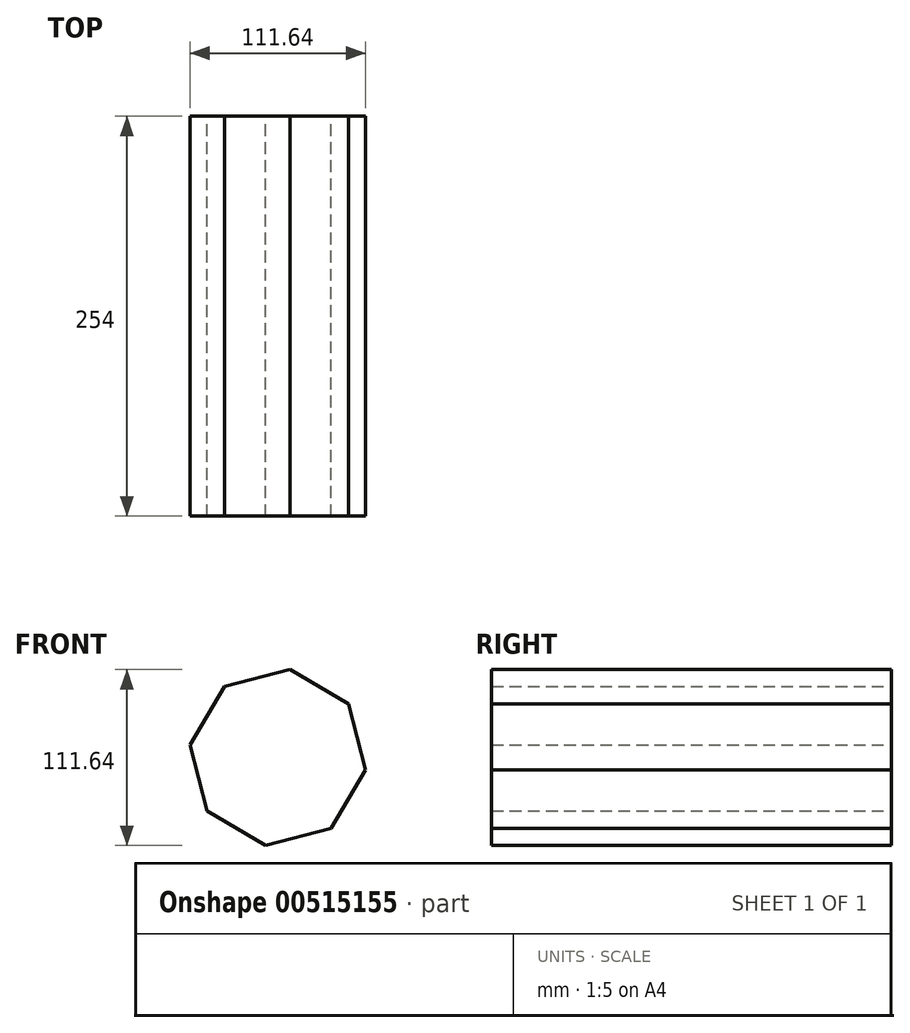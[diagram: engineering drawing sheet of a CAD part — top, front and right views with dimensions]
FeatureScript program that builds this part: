
annotation { "Feature Type Name" : "Feature", "Feature Type Description" : "" }
export const myFeature = defineFeature(function(context is Context, id is Id, definition is map)
    precondition{}
    {
        {
            var Q0;
            Q0=qCreatedBy(makeId("Front.planeOp"),FACE);
            var sketch = newSketch(context, id + "F0", { "sketchPlane" : qUnion([Q0])});
            skCircle(sketch, "E0.cCircle", {"center": v(0, 0) * mm, "radius": 56.37 * mm, "construction": true});
            skLineSegment(sketch, "E0.0", {"start": v(7.87, 55.82) * mm, "end": v(45.03, 33.9) * mm});
            skLineSegment(sketch, "E0.1", {"start": v(45.03, 33.9) * mm, "end": v(55.82, -7.87) * mm});
            skLineSegment(sketch, "E0.2", {"start": v(55.82, -7.87) * mm, "end": v(33.9, -45.03) * mm});
            skLineSegment(sketch, "E0.3", {"start": v(33.9, -45.03) * mm, "end": v(-7.87, -55.82) * mm});
            skLineSegment(sketch, "E0.4", {"start": v(-7.87, -55.82) * mm, "end": v(-45.03, -33.9) * mm});
            skLineSegment(sketch, "E0.5", {"start": v(-45.03, -33.9) * mm, "end": v(-55.82, 7.87) * mm});
            skLineSegment(sketch, "E0.6", {"start": v(-55.82, 7.87) * mm, "end": v(-33.9, 45.03) * mm});
            skLineSegment(sketch, "E0.7", {"start": v(-33.9, 45.03) * mm, "end": v(7.87, 55.82) * mm});
            skSolve(sketch);
        }
        {
            var Q0;
            Q0=qSketchRegion(id+"F0",true);
            extrude(context, id + "F1", {"entities" : qUnion([Q0]), "depth" : 254 * mm});
        }
    });
